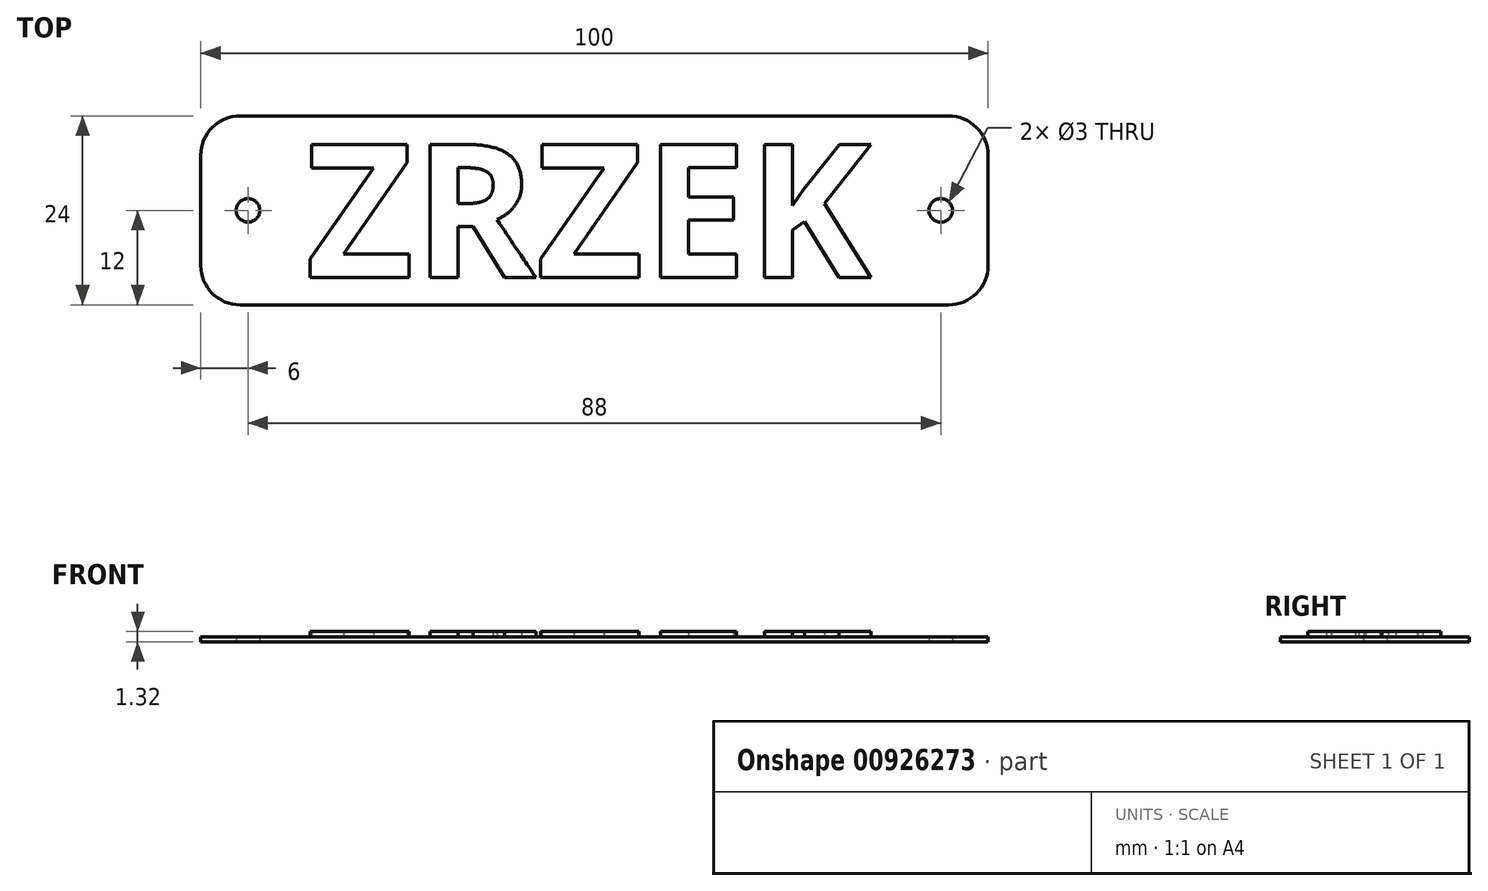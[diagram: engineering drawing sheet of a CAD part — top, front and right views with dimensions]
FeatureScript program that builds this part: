
annotation { "Feature Type Name" : "Feature", "Feature Type Description" : "" }
export const myFeature = defineFeature(function(context is Context, id is Id, definition is map)
    precondition{}
    {
        {
            var Q0;
            Q0=qCreatedBy(makeId("Top.planeOp"),FACE);
            var sketch = newSketch(context, id + "F0", { "sketchPlane" : qUnion([Q0])});
            skLineSegment(sketch, "E0.bottom", {"start": v(-45, 12) * mm, "end": v(45, 12) * mm});
            skLineSegment(sketch, "E0.top", {"start": v(-45, -12) * mm, "end": v(45, -12) * mm});
            skLineSegment(sketch, "E0.left", {"start": v(-50, 7) * mm, "end": v(-50, -7) * mm});
            skLineSegment(sketch, "E0.right", {"start": v(50, 7) * mm, "end": v(50, -7) * mm});
            skPoint(sketch, "E1.visualSharp", {"position": v(-50, 12) * mm});
            skArc(sketch, "E1.filletArc", {"start": v(-45, 12) * mm, "mid": v(-48.54, 10.54) * mm, "end": v(-50, 7) * mm});
            skPoint(sketch, "E2.visualSharp", {"position": v(-50, -12) * mm});
            skArc(sketch, "E2.filletArc", {"start": v(-50, -7) * mm, "mid": v(-48.54, -10.54) * mm, "end": v(-45, -12) * mm});
            skPoint(sketch, "E3.visualSharp", {"position": v(50, 12) * mm});
            skArc(sketch, "E3.filletArc", {"start": v(50, 7) * mm, "mid": v(48.54, 10.54) * mm, "end": v(45, 12) * mm});
            skPoint(sketch, "E4.visualSharp", {"position": v(50, -12) * mm});
            skArc(sketch, "E4.filletArc", {"start": v(45, -12) * mm, "mid": v(48.54, -10.54) * mm, "end": v(50, -7) * mm});
            skCircle(sketch, "E5", {"center": v(-44, 0) * mm, "radius": 1.5 * mm});
            skCircle(sketch, "E6", {"center": v(44, 0) * mm, "radius": 1.5 * mm});
            skText(sketch, "E7", { "text": "ZRZEK", "fontName": "OpenSans-Bold.ttf"});
            const initialGuessF0  = {"E7": [-0.03668, -0.0085, 1, 0, 0.017]};
            skSetInitialGuess(sketch, initialGuessF0);
            skSolve(sketch);
        }
        {
            var Q0;
            Q0 = qSketchRegion(id + "F0", true);
            var Q1;
            Q1=makeQuery(id+"F0.imprint","IMPRINT",FACE,{"disambiguationData":[TD([[makeQuery(id+"F0.imprint","IMPRINT",EDGE,{"derivedFrom":sQuery(id+"F0.wireOp",EDGE,"E7.sketch_text.stroke-10")}),1.0]])]});
            var Q2;
            Q2=makeQuery(id+"F0.imprint","IMPRINT",FACE,{"disambiguationData":[TD([[makeQuery(id+"F0.imprint","IMPRINT",EDGE,{"derivedFrom":sQuery(id+"F0.wireOp",EDGE,"E7.sketch_text.stroke-10")}),-1.0]])]});
            var Q3;
            Q3=makeQuery(id+"F0.imprint","IMPRINT",FACE,{"disambiguationData":[TD([[makeQuery(id+"F0.imprint","IMPRINT",EDGE,{"derivedFrom":sQuery(id+"F0.wireOp",EDGE,"E7.sketch_text.stroke-0")}),-1.0]])]});
            var Q4;
            Q4=makeQuery(id+"F0.imprint","IMPRINT",FACE,{"disambiguationData":[TD([[makeQuery(id+"F0.imprint","IMPRINT",EDGE,{"derivedFrom":sQuery(id+"F0.wireOp",EDGE,"E7.sketch_text.stroke-29")}),-1.0]])]});
            var Q5;
            Q5=makeQuery(id+"F0.imprint","IMPRINT",FACE,{"disambiguationData":[TD([[makeQuery(id+"F0.imprint","IMPRINT",EDGE,{"derivedFrom":sQuery(id+"F0.wireOp",EDGE,"E7.sketch_text.stroke-39")}),-1.0]])]});
            var Q6;
            Q6=makeQuery(id+"F0.imprint","IMPRINT",FACE,{"disambiguationData":[TD([[makeQuery(id+"F0.imprint","IMPRINT",EDGE,{"derivedFrom":sQuery(id+"F0.wireOp",EDGE,"E7.sketch_text.stroke-51")}),-1.0]])]});
            extrude(context, id + "F1", {"entities" : qUnion([Q0, Q1, Q2, Q3, Q4, Q5, Q6]), "depth" : 0.66 * mm, "offsetDistance" : 25 * mm});
        }
        {
            var Q0;
            Q0=makeQuery(id+"F0.imprint","IMPRINT",FACE,{"disambiguationData":[TD([[makeQuery(id+"F0.imprint","IMPRINT",EDGE,{"derivedFrom":sQuery(id+"F0.wireOp",EDGE,"E7.sketch_text.stroke-0")}),-1.0]])]});
            var Q1;
            Q1=makeQuery(id+"F0.imprint","IMPRINT",FACE,{"disambiguationData":[TD([[makeQuery(id+"F0.imprint","IMPRINT",EDGE,{"derivedFrom":sQuery(id+"F0.wireOp",EDGE,"E7.sketch_text.stroke-10")}),-1.0]])]});
            var Q2;
            Q2=makeQuery(id+"F0.imprint","IMPRINT",FACE,{"disambiguationData":[TD([[makeQuery(id+"F0.imprint","IMPRINT",EDGE,{"derivedFrom":sQuery(id+"F0.wireOp",EDGE,"E7.sketch_text.stroke-29")}),-1.0]])]});
            var Q3;
            Q3=makeQuery(id+"F0.imprint","IMPRINT",FACE,{"disambiguationData":[TD([[makeQuery(id+"F0.imprint","IMPRINT",EDGE,{"derivedFrom":sQuery(id+"F0.wireOp",EDGE,"E7.sketch_text.stroke-39")}),-1.0]])]});
            var Q4;
            Q4=makeQuery(id+"F0.imprint","IMPRINT",FACE,{"disambiguationData":[TD([[makeQuery(id+"F0.imprint","IMPRINT",EDGE,{"derivedFrom":sQuery(id+"F0.wireOp",EDGE,"E7.sketch_text.stroke-51")}),-1.0]])]});
            extrude(context, id + "F2", {"entities" : qUnion([Q0, Q1, Q2, Q3, Q4]), "operationType" : NewBodyOperationType.ADD, "depth" : (0.66 * 2) * mm, "offsetDistance" : 25 * mm});
        }
    });
